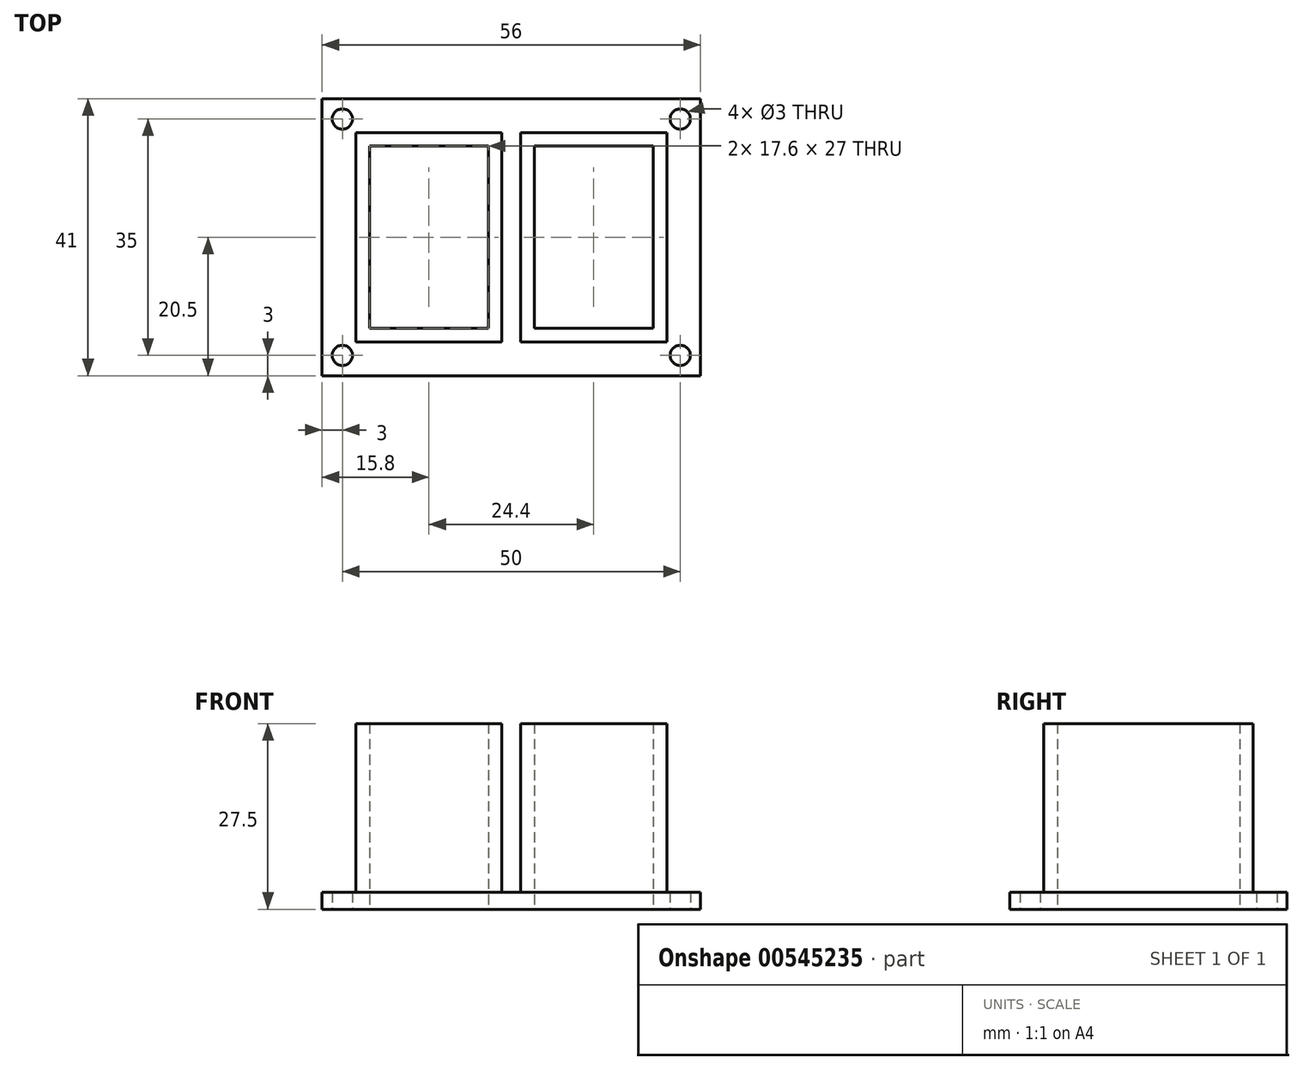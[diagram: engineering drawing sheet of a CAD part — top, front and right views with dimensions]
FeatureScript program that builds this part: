
annotation { "Feature Type Name" : "Feature", "Feature Type Description" : "" }
export const myFeature = defineFeature(function(context is Context, id is Id, definition is map)
    precondition{}
    {
        {
            var Q0;
            Q0=qCreatedBy(makeId("Top.planeOp"),FACE);
            var sketch = newSketch(context, id + "F0", { "sketchPlane" : qUnion([Q0])});
            skPoint(sketch, "E0.middle", {"position": v(0, 0) * mm});
            skLineSegment(sketch, "E1.0", {"start": v(21, 13.5) * mm, "end": v(3.4, 13.5) * mm});
            skLineSegment(sketch, "E1.1", {"start": v(21, 13.5) * mm, "end": v(21, -13.5) * mm});
            skLineSegment(sketch, "E1.2", {"start": v(21, -13.5) * mm, "end": v(3.4, -13.5) * mm});
            skLineSegment(sketch, "E1.3", {"start": v(-21, 13.5) * mm, "end": v(-21, -13.5) * mm});
            skLineSegment(sketch, "E2", {"start": v(3.4, 0) * mm, "end": v(3.4, 13.5) * mm});
            skLineSegment(sketch, "E3", {"start": v(3.4, 0) * mm, "end": v(3.4, -13.5) * mm});
            skLineSegment(sketch, "E4", {"start": v(-3.4, 0) * mm, "end": v(-3.4, 13.5) * mm});
            skLineSegment(sketch, "E5", {"start": v(-3.4, 0) * mm, "end": v(-3.4, -13.5) * mm});
            skLineSegment(sketch, "E6.trimOffspring", {"start": v(-3.4, 13.5) * mm, "end": v(-21, 13.5) * mm});
            skLineSegment(sketch, "E7.trimOffspring", {"start": v(-3.4, -13.5) * mm, "end": v(-21, -13.5) * mm});
            skLineSegment(sketch, "E8.0", {"start": v(28, 20.5) * mm, "end": v(-28, 20.5) * mm});
            skLineSegment(sketch, "E8.1", {"start": v(28, 20.5) * mm, "end": v(28, -20.5) * mm});
            skLineSegment(sketch, "E8.2", {"start": v(28, -20.5) * mm, "end": v(-28, -20.5) * mm});
            skLineSegment(sketch, "E8.3", {"start": v(-28, 20.5) * mm, "end": v(-28, -20.5) * mm});
            skCircle(sketch, "E9", {"center": v(-25, 17.5) * mm, "radius": 1.5 * mm});
            skCircle(sketch, "E10", {"center": v(25, 17.5) * mm, "radius": 1.5 * mm});
            skCircle(sketch, "E11", {"center": v(25, -17.5) * mm, "radius": 1.5 * mm});
            skCircle(sketch, "E12", {"center": v(-25, -17.5) * mm, "radius": 1.5 * mm});
            skSolve(sketch);
        }
        {
            var Q0;
            Q0 = qSketchRegion(id + "F0", true);
            extrude(context, id + "F1", {"entities" : qUnion([Q0]), "depth" : 2.5 * mm, "offsetDistance" : 25 * mm});
        }
        {
            var Q0;
            Q0=makeQuery(id+"F1.opExtrude","CAP_FACE",FACE,{"disambiguationData":[OSD([sQuery(id+"F0.wireOp",EDGE,"E1.0"),sQuery(id+"F0.wireOp",EDGE,"E1.1"),sQuery(id+"F0.wireOp",EDGE,"E1.2"),sQuery(id+"F0.wireOp",EDGE,"E1.3"),sQuery(id+"F0.wireOp",EDGE,"E2"),sQuery(id+"F0.wireOp",EDGE,"E3"),sQuery(id+"F0.wireOp",EDGE,"E4"),sQuery(id+"F0.wireOp",EDGE,"E5"),sQuery(id+"F0.wireOp",EDGE,"E6.trimOffspring"),sQuery(id+"F0.wireOp",EDGE,"E7.trimOffspring"),sQuery(id+"F0.wireOp",EDGE,"E8.0"),sQuery(id+"F0.wireOp",EDGE,"E8.1"),sQuery(id+"F0.wireOp",EDGE,"E8.2"),sQuery(id+"F0.wireOp",EDGE,"E8.3"),sQuery(id+"F0.wireOp",EDGE,"E9"),sQuery(id+"F0.wireOp",EDGE,"E10"),sQuery(id+"F0.wireOp",EDGE,"E11"),sQuery(id+"F0.wireOp",EDGE,"E12")])],"isStart":false});
            var sketch = newSketch(context, id + "F2", { "sketchPlane" : qUnion([Q0])});
            skLineSegment(sketch, "E13.0", {"start": v(-23, 15.5) * mm, "end": v(-23, -15.5) * mm});
            skLineSegment(sketch, "E13.1", {"start": v(-1.4, 15.5) * mm, "end": v(-23, 15.5) * mm});
            skLineSegment(sketch, "E13.2", {"start": v(-1.4, -15.5) * mm, "end": v(-1.4, 15.5) * mm});
            skLineSegment(sketch, "E13.3", {"start": v(-1.4, -15.5) * mm, "end": v(-23, -15.5) * mm});
            skLineSegment(sketch, "E14.0", {"start": v(1.4, 15.5) * mm, "end": v(1.4, -15.5) * mm});
            skLineSegment(sketch, "E14.1", {"start": v(23, 15.5) * mm, "end": v(1.4, 15.5) * mm});
            skLineSegment(sketch, "E14.2", {"start": v(23, 15.5) * mm, "end": v(23, -15.5) * mm});
            skLineSegment(sketch, "E14.3", {"start": v(23, -15.5) * mm, "end": v(1.4, -15.5) * mm});
            skSolve(sketch);
        }
        {
            var Q0;
            Q0=makeQuery(id+"F2.imprint","IMPRINT",FACE,{"disambiguationData":[TD([[makeQuery(id+"F2.imprint","IMPRINT",EDGE,{"derivedFrom":sQuery(id+"F2.wireOp",EDGE,"E13.0")}),1.0]])]});
            var Q1;
            Q1=makeQuery(id+"F2.imprint","IMPRINT",FACE,{"disambiguationData":[TD([[makeQuery(id+"F2.imprint","IMPRINT",EDGE,{"derivedFrom":sQuery(id+"F2.wireOp",EDGE,"E14.0")}),1.0]])]});
            extrude(context, id + "F3", {"entities" : qUnion([Q0, Q1]), "operationType" : NewBodyOperationType.ADD, "depth" : 25 * mm, "offsetDistance" : 25 * mm});
        }
    });
